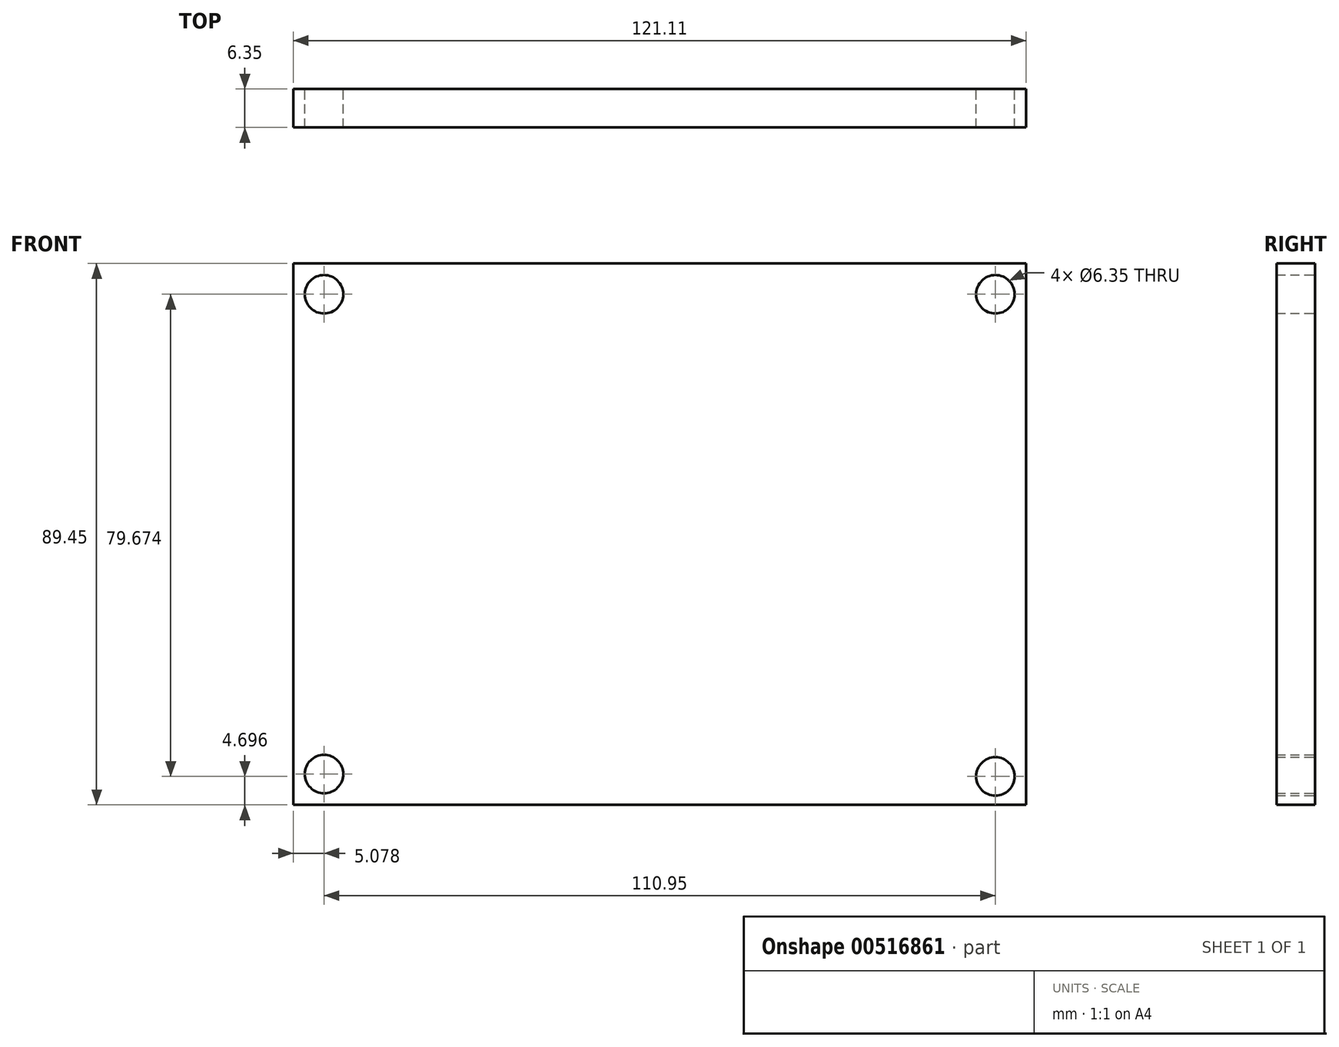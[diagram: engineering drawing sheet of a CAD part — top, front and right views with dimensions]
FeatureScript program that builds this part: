
annotation { "Feature Type Name" : "Feature", "Feature Type Description" : "" }
export const myFeature = defineFeature(function(context is Context, id is Id, definition is map)
    precondition{}
    {
        {
            var Q0;
            Q0=qCreatedBy(makeId("Front.planeOp"),FACE);
            var sketch = newSketch(context, id + "F0", { "sketchPlane" : qUnion([Q0])});
            skLineSegment(sketch, "E0.bottom", {"start": v(-75.85, 41.6) * mm, "end": v(45.26, 41.6) * mm});
            skLineSegment(sketch, "E0.top", {"start": v(-75.85, -47.84) * mm, "end": v(45.26, -47.84) * mm});
            skLineSegment(sketch, "E0.left", {"start": v(-75.85, 41.6) * mm, "end": v(-75.85, -47.84) * mm});
            skLineSegment(sketch, "E0.right", {"start": v(45.26, 41.6) * mm, "end": v(45.26, -47.84) * mm});
            skCircle(sketch, "E1", {"center": v(-70.77, 36.53) * mm, "radius": 3.18 * mm});
            skCircle(sketch, "E2", {"center": v(40.18, 36.53) * mm, "radius": 3.18 * mm});
            skCircle(sketch, "E3", {"center": v(-70.77, -42.76) * mm, "radius": 3.18 * mm});
            skCircle(sketch, "E4", {"center": v(40.18, -43.14) * mm, "radius": 3.18 * mm});
            skSolve(sketch);
        }
        {
            var Q0;
            Q0 = qSketchRegion(id + "F0", true);
            extrude(context, id + "F1", {"entities" : qUnion([Q0]), "depth" : 6.35 * mm, "offsetDistance" : 25.4 * mm});
        }
    });
